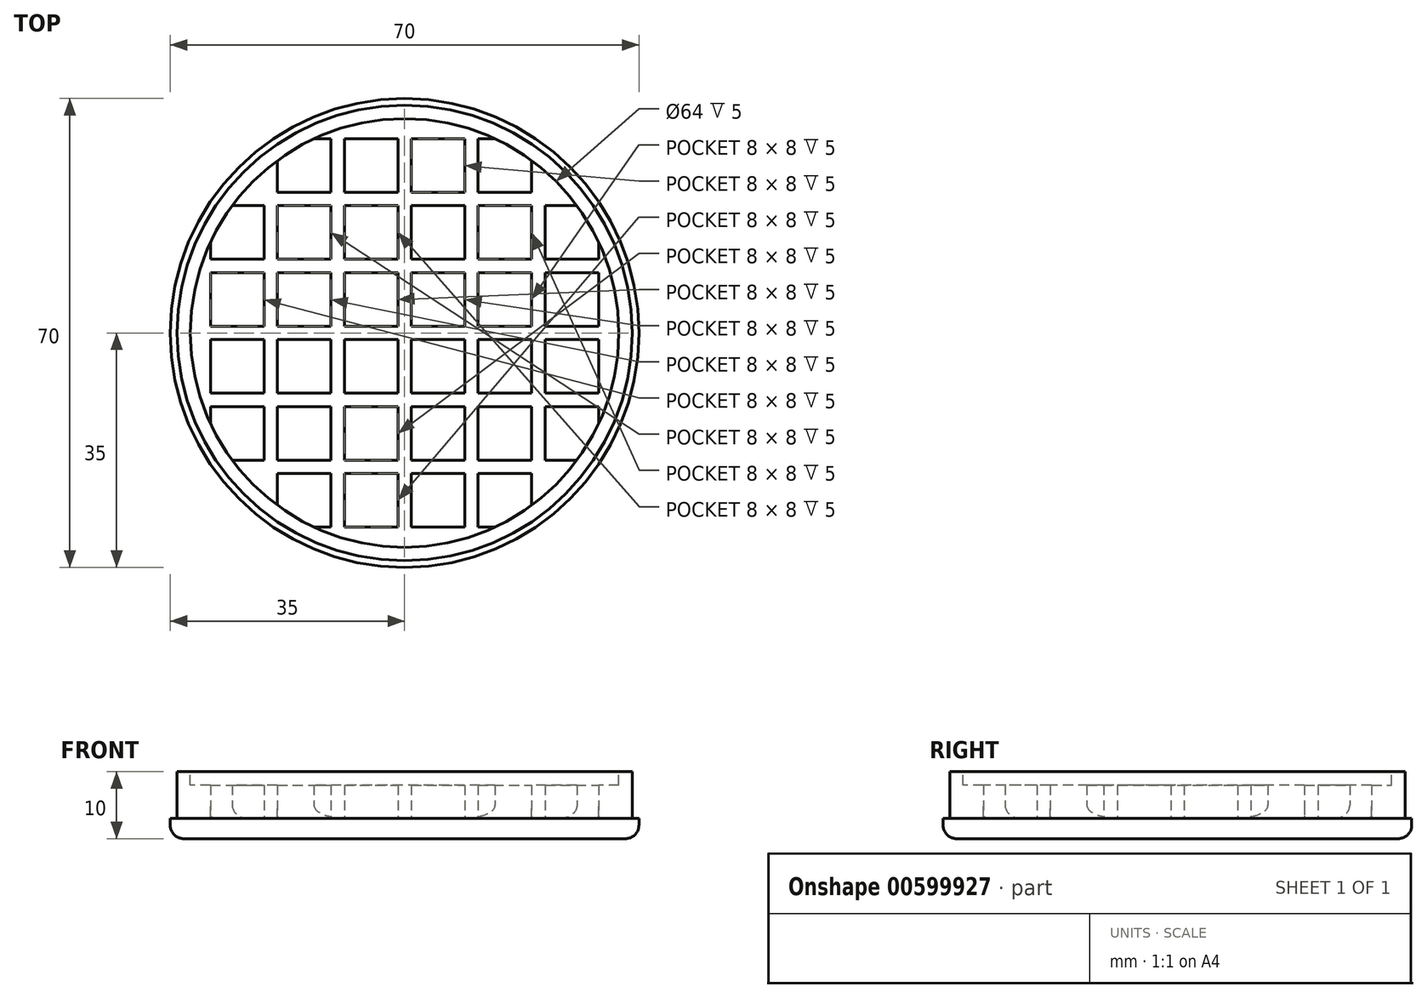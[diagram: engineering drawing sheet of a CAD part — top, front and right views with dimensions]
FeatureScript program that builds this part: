
annotation { "Feature Type Name" : "Feature", "Feature Type Description" : "" }
export const myFeature = defineFeature(function(context is Context, id is Id, definition is map)
    precondition{}
    {
        {
            var Q0;
            Q0=qCreatedBy(makeId("Front.planeOp"),FACE);
            var sketch = newSketch(context, id + "F0", { "sketchPlane" : qUnion([Q0])});
            skLineSegment(sketch, "E0", {"start": v(0, 0) * mm, "end": v(-33, 0) * mm});
            skLineSegment(sketch, "E1", {"start": v(-35, 2) * mm, "end": v(-35, 3) * mm});
            skLineSegment(sketch, "E2", {"start": v(-35, 3) * mm, "end": v(-34, 3) * mm});
            skLineSegment(sketch, "E3", {"start": v(-34, 3) * mm, "end": v(-34, 10) * mm});
            skLineSegment(sketch, "E4", {"start": v(-34, 10) * mm, "end": v(-32, 10) * mm});
            skLineSegment(sketch, "E5", {"start": v(0, 3) * mm, "end": v(0, 0) * mm});
            skPoint(sketch, "E6.visualSharp", {"position": v(-32, 3) * mm});
            skPoint(sketch, "E7.visualSharp", {"position": v(-35, 0) * mm});
            skArc(sketch, "E7.filletArc", {"start": v(-35, 2) * mm, "mid": v(-34.41, 0.59) * mm, "end": v(-33, 0) * mm});
            skLineSegment(sketch, "E8", {"start": v(-32, 10) * mm, "end": v(-32, 3) * mm});
            skLineSegment(sketch, "E9", {"start": v(-32, 3) * mm, "end": v(0, 3) * mm});
            skSolve(sketch);
        }
        {
            var Q0;
            Q0=makeQuery(id+"F0.imprint","IMPRINT",FACE,{"disambiguationData":[TD([[makeQuery(id+"F0.imprint","IMPRINT",EDGE,{"derivedFrom":sQuery(id+"F0.wireOp",EDGE,"E0")}),-1.0]])]});
            var Q1;
            Q1=sQuery(id+"F0.wireOp",EDGE,"E5");
            revolve(context, id + "F1", {"entities" : qUnion([Q0]), "axis" : qUnion([Q1]), "revolveType" : RevolveType.FULL});
        }
        {
            var Q0;
            Q0=makeQuery(id+"F1.opRevolve","SWEPT_FACE",FACE,{"disambiguationData":[OSD([sQuery(id+"F0.wireOp",EDGE,"E9")])]});
            var sketch = newSketch(context, id + "F2", { "sketchPlane" : qUnion([Q0])});
            skLineSegment(sketch, "E10", {"start": v(0, 32) * mm, "end": v(0, 19) * mm, "construction": true});
            skLineSegment(sketch, "E11", {"start": v(-46.87, 0) * mm, "end": v(0, 0) * mm, "construction": true});
            skLineSegment(sketch, "E12.trimOffspring", {"start": v(9, 29) * mm, "end": v(9, 21) * mm});
            skLineSegment(sketch, "E13.trimOffspring", {"start": v(11, 29) * mm, "end": v(13.53, 29) * mm});
            skLineSegment(sketch, "E14.trimOffspring", {"start": v(19, 25.75) * mm, "end": v(19, 21) * mm});
            skLineSegment(sketch, "E15.trimOffspring", {"start": v(29, 13.53) * mm, "end": v(29, 11) * mm});
            skLineSegment(sketch, "E16.trimOffspring", {"start": v(19, 19) * mm, "end": v(19, 11) * mm});
            skLineSegment(sketch, "E17.trimOffspring", {"start": v(21, 19) * mm, "end": v(21, 11) * mm});
            skLineSegment(sketch, "E18.trimOffspring", {"start": v(0, 11) * mm, "end": v(0, -20.11) * mm, "construction": true});
            skLineSegment(sketch, "E19.trimOffspring", {"start": v(11, 19) * mm, "end": v(11, 11) * mm});
            skLineSegment(sketch, "E20.trimOffspring", {"start": v(21, 19) * mm, "end": v(25.75, 19) * mm});
            skLineSegment(sketch, "E21.trimOffspring", {"start": v(9, 9) * mm, "end": v(9, 1) * mm});
            skLineSegment(sketch, "E22.trimOffspring", {"start": v(11, 19) * mm, "end": v(19, 19) * mm});
            skLineSegment(sketch, "E23", {"start": v(11, 29) * mm, "end": v(11, 21) * mm});
            skLineSegment(sketch, "E24.trimOffspring", {"start": v(11, 21) * mm, "end": v(19, 21) * mm});
            skLineSegment(sketch, "E25.trimOffspring", {"start": v(1, 21) * mm, "end": v(9, 21) * mm});
            skLineSegment(sketch, "E26.trimOffspring", {"start": v(1, 19) * mm, "end": v(1, 11) * mm});
            skLineSegment(sketch, "E27.trimOffspring", {"start": v(-1, 19) * mm, "end": v(-1, 11) * mm});
            skLineSegment(sketch, "E28.trimOffspring", {"start": v(1, 19) * mm, "end": v(9, 19) * mm});
            skLineSegment(sketch, "E29.trimOffspring", {"start": v(-9, 21) * mm, "end": v(-1, 21) * mm});
            skLineSegment(sketch, "E30.trimOffspring", {"start": v(-11, 19) * mm, "end": v(-11, 11) * mm});
            skLineSegment(sketch, "E31.trimOffspring", {"start": v(-9, 19) * mm, "end": v(-1, 19) * mm});
            skLineSegment(sketch, "E32.trimOffspring", {"start": v(-9, 19) * mm, "end": v(-9, 11) * mm});
            skLineSegment(sketch, "E33.trimOffspring", {"start": v(-9, 29) * mm, "end": v(-9, 21) * mm});
            skLineSegment(sketch, "E34.trimOffspring", {"start": v(-9, 29) * mm, "end": v(-1, 29) * mm});
            skLineSegment(sketch, "E35.trimOffspring", {"start": v(-11, 29) * mm, "end": v(-11, 21) * mm});
            skLineSegment(sketch, "E36.trimOffspring", {"start": v(-9, 11) * mm, "end": v(-1, 11) * mm});
            skLineSegment(sketch, "E37.trimOffspring", {"start": v(-11, 9) * mm, "end": v(-11, 1) * mm});
            skLineSegment(sketch, "E38.trimOffspring", {"start": v(-9, 9) * mm, "end": v(-9, 1) * mm});
            skLineSegment(sketch, "E39", {"start": v(-19, 9) * mm, "end": v(-11, 9) * mm});
            skLineSegment(sketch, "E40.trimOffspring", {"start": v(-19, 11) * mm, "end": v(-11, 11) * mm});
            skLineSegment(sketch, "E41.trimOffspring", {"start": v(-21, 9) * mm, "end": v(-21, 1) * mm});
            skLineSegment(sketch, "E42.trimOffspring", {"start": v(-19, 9) * mm, "end": v(-19, 1) * mm});
            skLineSegment(sketch, "E43.trimOffspring", {"start": v(-29, 11) * mm, "end": v(-21, 11) * mm});
            skLineSegment(sketch, "E44.trimOffspring", {"start": v(-29, 9) * mm, "end": v(-29, 1) * mm});
            skLineSegment(sketch, "E45.trimOffspring", {"start": v(-29, 9) * mm, "end": v(-21, 9) * mm});
            skLineSegment(sketch, "E46.trimOffspring", {"start": v(-25.75, 19) * mm, "end": v(-21, 19) * mm});
            skLineSegment(sketch, "E47.trimOffspring", {"start": v(-29, 13.53) * mm, "end": v(-29, 11) * mm});
            skPoint(sketch, "E48.MirrorCS.start.orphan", {"position": v(-27.7, 31) * mm});
            skLineSegment(sketch, "E49.trimOffspring", {"start": v(-13.53, 29) * mm, "end": v(-11, 29) * mm});
            skLineSegment(sketch, "E50.trimOffspring", {"start": v(-19, 25.75) * mm, "end": v(-19, 21) * mm});
            skLineSegment(sketch, "E51.trimOffspring", {"start": v(29, -1) * mm, "end": v(29, -9) * mm});
            skLineSegment(sketch, "E52.trimOffspring", {"start": v(29, 9) * mm, "end": v(29, 1) * mm});
            skLineSegment(sketch, "E53.trimOffspring", {"start": v(21, 9) * mm, "end": v(21, 1) * mm});
            skLineSegment(sketch, "E54.trimOffspring", {"start": v(21, 11) * mm, "end": v(29, 11) * mm});
            skLineSegment(sketch, "E55.trimOffspring", {"start": v(19, 9) * mm, "end": v(19, 1) * mm});
            skLineSegment(sketch, "E56.trimOffspring", {"start": v(21, 9) * mm, "end": v(29, 9) * mm});
            skLineSegment(sketch, "E57", {"start": v(9, 11) * mm, "end": v(9, 19) * mm});
            skLineSegment(sketch, "E58.trimOffspring", {"start": v(11, 9) * mm, "end": v(11, 1) * mm});
            skLineSegment(sketch, "E59.trimOffspring", {"start": v(11, 11) * mm, "end": v(19, 11) * mm});
            skLineSegment(sketch, "E60.trimOffspring", {"start": v(11, 9) * mm, "end": v(19, 9) * mm});
            skLineSegment(sketch, "E61.trimOffspring", {"start": v(1, 11) * mm, "end": v(9, 11) * mm});
            skLineSegment(sketch, "E62.trimOffspring", {"start": v(1, 9) * mm, "end": v(9, 9) * mm});
            skLineSegment(sketch, "E63.trimOffspring", {"start": v(1, 9) * mm, "end": v(1, 1) * mm});
            skLineSegment(sketch, "E64.trimOffspring", {"start": v(-1, 9) * mm, "end": v(-1, 1) * mm});
            skLineSegment(sketch, "E65", {"start": v(-19, 21) * mm, "end": v(-11, 21) * mm});
            skLineSegment(sketch, "E66.trimOffspring", {"start": v(-21, 19) * mm, "end": v(-21, 11) * mm});
            skLineSegment(sketch, "E67.trimOffspring", {"start": v(-19, 19) * mm, "end": v(-11, 19) * mm});
            skLineSegment(sketch, "E68.trimOffspring", {"start": v(-19, 19) * mm, "end": v(-19, 11) * mm});
            skLineSegment(sketch, "E69.trimOffspring", {"start": v(-29, 1) * mm, "end": v(-21, 1) * mm});
            skLineSegment(sketch, "E70.trimOffspring", {"start": v(-29, -1) * mm, "end": v(-29, -9) * mm});
            skPoint(sketch, "E71.MirrorCS.start.orphan", {"position": v(-33.6, 29) * mm});
            skLineSegment(sketch, "E72.trimOffspring", {"start": v(-29, -9) * mm, "end": v(-21, -9) * mm});
            skLineSegment(sketch, "E73.trimOffspring", {"start": v(-29, -11) * mm, "end": v(-29, -13.53) * mm});
            skLineSegment(sketch, "E74.trimOffspring", {"start": v(-29, -11) * mm, "end": v(-21, -11) * mm});
            skLineSegment(sketch, "E75.trimOffspring", {"start": v(-25.75, -19) * mm, "end": v(-21, -19) * mm});
            skLineSegment(sketch, "E76.trimOffspring", {"start": v(-13.53, -29) * mm, "end": v(-11, -29) * mm});
            skLineSegment(sketch, "E77.trimOffspring", {"start": v(-19, -21) * mm, "end": v(-11, -21) * mm});
            skLineSegment(sketch, "E78.trimOffspring", {"start": v(-19, -21) * mm, "end": v(-19, -25.75) * mm});
            skLineSegment(sketch, "E79.trimOffspring", {"start": v(-19, -19) * mm, "end": v(-11, -19) * mm});
            skLineSegment(sketch, "E80.trimOffspring", {"start": v(-21, -1) * mm, "end": v(-21, -9) * mm});
            skLineSegment(sketch, "E81.trimOffspring", {"start": v(-19, 1) * mm, "end": v(-11, 1) * mm});
            skLineSegment(sketch, "E82.trimOffspring", {"start": v(-19, -1) * mm, "end": v(-19, -9) * mm});
            skLineSegment(sketch, "E83.trimOffspring", {"start": v(-19, -1) * mm, "end": v(-11, -1) * mm});
            skLineSegment(sketch, "E84.trimOffspring", {"start": v(-11, -1) * mm, "end": v(-11, -9) * mm});
            skLineSegment(sketch, "E85.trimOffspring", {"start": v(-9, -1) * mm, "end": v(-9, -9) * mm});
            skLineSegment(sketch, "E86.trimOffspring", {"start": v(-9, -1) * mm, "end": v(-1, -1) * mm});
            skLineSegment(sketch, "E87.trimOffspring", {"start": v(-1, -11) * mm, "end": v(-1, -19) * mm});
            skLineSegment(sketch, "E88.trimOffspring", {"start": v(1, 1) * mm, "end": v(9, 1) * mm});
            skLineSegment(sketch, "E89.trimOffspring", {"start": v(1, -1) * mm, "end": v(1, -9) * mm});
            skLineSegment(sketch, "E90.trimOffspring", {"start": v(1, -1) * mm, "end": v(9, -1) * mm});
            skLineSegment(sketch, "E91", {"start": v(-9, 9) * mm, "end": v(-1, 9) * mm});
            skLineSegment(sketch, "E92", {"start": v(-9, 1) * mm, "end": v(-1, 1) * mm});
            skLineSegment(sketch, "E93", {"start": v(-1, -1) * mm, "end": v(-1, -9) * mm});
            skLineSegment(sketch, "E94.trimOffspring", {"start": v(1, -9) * mm, "end": v(9, -9) * mm});
            skLineSegment(sketch, "E95.trimOffspring", {"start": v(1, -11) * mm, "end": v(1, -19) * mm});
            skLineSegment(sketch, "E96.trimOffspring", {"start": v(1, -11) * mm, "end": v(9, -11) * mm});
            skLineSegment(sketch, "E97.trimOffspring", {"start": v(-11, -11) * mm, "end": v(-11, -19) * mm});
            skLineSegment(sketch, "E98.trimOffspring", {"start": v(-9, -9) * mm, "end": v(-1, -9) * mm});
            skLineSegment(sketch, "E99.trimOffspring", {"start": v(-9, -11) * mm, "end": v(-9, -19) * mm});
            skLineSegment(sketch, "E100.trimOffspring", {"start": v(-9, -11) * mm, "end": v(-1, -11) * mm});
            skLineSegment(sketch, "E101.trimOffspring", {"start": v(-1, -21) * mm, "end": v(-1, -29) * mm});
            skLineSegment(sketch, "E102.trimOffspring", {"start": v(1, -19) * mm, "end": v(9, -19) * mm});
            skLineSegment(sketch, "E103.trimOffspring", {"start": v(1, -21) * mm, "end": v(1, -29) * mm});
            skLineSegment(sketch, "E104.trimOffspring", {"start": v(1, -21) * mm, "end": v(9, -21) * mm});
            skLineSegment(sketch, "E105.trimOffspring", {"start": v(-9, -19) * mm, "end": v(-1, -19) * mm});
            skLineSegment(sketch, "E106.trimOffspring", {"start": v(-9, -21) * mm, "end": v(-9, -29) * mm});
            skLineSegment(sketch, "E107.trimOffspring", {"start": v(-9, -21) * mm, "end": v(-1, -21) * mm});
            skLineSegment(sketch, "E108.trimOffspring", {"start": v(-11, -21) * mm, "end": v(-11, -29) * mm});
            skLineSegment(sketch, "E109.trimOffspring", {"start": v(-9, -29) * mm, "end": v(-1, -29) * mm});
            skLineSegment(sketch, "E110.trimOffspring", {"start": v(1, -29) * mm, "end": v(9, -29) * mm});
            skLineSegment(sketch, "E111.trimOffspring", {"start": v(-21, -11) * mm, "end": v(-21, -19) * mm});
            skLineSegment(sketch, "E112.trimOffspring", {"start": v(-19, -9) * mm, "end": v(-11, -9) * mm});
            skLineSegment(sketch, "E113.trimOffspring", {"start": v(-19, -11) * mm, "end": v(-19, -19) * mm});
            skLineSegment(sketch, "E114.trimOffspring", {"start": v(-19, -11) * mm, "end": v(-11, -11) * mm});
            skLineSegment(sketch, "E115.trimOffspring", {"start": v(1, 29) * mm, "end": v(1, 21) * mm});
            skLineSegment(sketch, "E116.trimOffspring", {"start": v(1, 29) * mm, "end": v(9, 29) * mm});
            skLineSegment(sketch, "E117.trimOffspring", {"start": v(11, 1) * mm, "end": v(19, 1) * mm});
            skLineSegment(sketch, "E118.trimOffspring", {"start": v(9, -1) * mm, "end": v(9, -9) * mm});
            skLineSegment(sketch, "E119.trimOffspring", {"start": v(11, -1) * mm, "end": v(11, -9) * mm});
            skLineSegment(sketch, "E120.trimOffspring", {"start": v(11, -1) * mm, "end": v(19, -1) * mm});
            skLineSegment(sketch, "E121.trimOffspring", {"start": v(19, -1) * mm, "end": v(19, -9) * mm});
            skLineSegment(sketch, "E122.trimOffspring", {"start": v(21, -1) * mm, "end": v(29, -1) * mm});
            skLineSegment(sketch, "E123.trimOffspring", {"start": v(21, -1) * mm, "end": v(21, -9) * mm});
            skLineSegment(sketch, "E124.trimOffspring", {"start": v(21, 1) * mm, "end": v(29, 1) * mm});
            skLineSegment(sketch, "E125.trimOffspring", {"start": v(29, -11) * mm, "end": v(29, -13.53) * mm});
            skLineSegment(sketch, "E126.trimOffspring", {"start": v(21, -9) * mm, "end": v(29, -9) * mm});
            skLineSegment(sketch, "E127.trimOffspring", {"start": v(19, -11) * mm, "end": v(19, -19) * mm});
            skLineSegment(sketch, "E128.trimOffspring", {"start": v(21, -11) * mm, "end": v(29, -11) * mm});
            skLineSegment(sketch, "E129.trimOffspring", {"start": v(21, -11) * mm, "end": v(21, -19) * mm});
            skLineSegment(sketch, "E130.trimOffspring", {"start": v(21, -19) * mm, "end": v(25.75, -19) * mm});
            skLineSegment(sketch, "E131.trimOffspring", {"start": v(19, -21) * mm, "end": v(19, -25.75) * mm});
            skPoint(sketch, "E132.orphan", {"position": v(21, -41.31) * mm});
            skLineSegment(sketch, "E133.trimOffspring", {"start": v(11, -29) * mm, "end": v(13.53, -29) * mm});
            skLineSegment(sketch, "E134.trimOffspring", {"start": v(11, -19) * mm, "end": v(19, -19) * mm});
            skLineSegment(sketch, "E135.trimOffspring", {"start": v(11, -21) * mm, "end": v(11, -29) * mm});
            skLineSegment(sketch, "E136.trimOffspring", {"start": v(11, -21) * mm, "end": v(19, -21) * mm});
            skLineSegment(sketch, "E137.trimOffspring", {"start": v(9, -21) * mm, "end": v(9, -29) * mm});
            skLineSegment(sketch, "E138.trimOffspring", {"start": v(11, -9) * mm, "end": v(19, -9) * mm});
            skLineSegment(sketch, "E139.trimOffspring", {"start": v(9, -11) * mm, "end": v(9, -19) * mm});
            skLineSegment(sketch, "E140.trimOffspring", {"start": v(11, -11) * mm, "end": v(19, -11) * mm});
            skLineSegment(sketch, "E141.trimOffspring", {"start": v(11, -11) * mm, "end": v(11, -19) * mm});
            skLineSegment(sketch, "E142", {"start": v(-29, -1) * mm, "end": v(-21, -1) * mm});
            skArc(sketch, "E143", {"start": v(25.75, 19) * mm, "mid": v(22.63, 22.63) * mm, "end": v(19, 25.75) * mm});
            skLineSegment(sketch, "E144.trimOffspring", {"start": v(-1, 29) * mm, "end": v(-1, 21) * mm});
            skArc(sketch, "E145.trimOffspring", {"start": v(-29, 13.53) * mm, "mid": v(-32, 0) * mm, "end": v(-29, -13.53) * mm});
            skArc(sketch, "E146.trimOffspring", {"start": v(-19, 25.75) * mm, "mid": v(-22.63, 22.63) * mm, "end": v(-25.75, 19) * mm});
            skArc(sketch, "E147.trimOffspring", {"start": v(13.53, 29) * mm, "mid": v(0, 32) * mm, "end": v(-13.53, 29) * mm});
            skArc(sketch, "E148.1.0", {"start": v(19, -25.75) * mm, "mid": v(22.63, -22.63) * mm, "end": v(25.75, -19) * mm});
            skArc(sketch, "E148.1.1", {"start": v(-25.75, -19) * mm, "mid": v(-22.63, -22.63) * mm, "end": v(-19, -25.75) * mm});
            skArc(sketch, "E148.1.2", {"start": v(29, -13.53) * mm, "mid": v(32, 0) * mm, "end": v(29, 13.53) * mm});
            skArc(sketch, "E149.MirrorCS", {"start": v(13.53, -29) * mm, "mid": v(0, -32) * mm, "end": v(-13.53, -29) * mm});
            skPoint(sketch, "E150.MirrorCS.end.orphan", {"position": v(-13.53, -29) * mm});
            skPoint(sketch, "E150.MirrorCS.start.orphan", {"position": v(13.53, -29) * mm});
            skSolve(sketch);
        }
        {
            var Q0;
            Q0 = qSketchRegion(id + "F2", true);
            extrude(context, id + "F3", {"entities" : qUnion([Q0]), "operationType" : NewBodyOperationType.ADD, "depth" : 5 * mm, "offsetDistance" : 25 * mm});
        }
        {
            var Q0;
            Q0=makeQuery(id+"F3.opExtrude","CAP_EDGE",EDGE,{"disambiguationData":[OSD([sQuery(id+"F2.wireOp",EDGE,"E149.MirrorCS")])],"isStart":false});
            var Q1;
            Q1=makeQuery(id+"F3.opExtrude","CAP_EDGE",EDGE,{"disambiguationData":[OSD([sQuery(id+"F2.wireOp",EDGE,"E148.1.1")])],"isStart":false});
            var Q2;
            Q2=makeQuery(id+"F3.opExtrude","CAP_EDGE",EDGE,{"disambiguationData":[OSD([sQuery(id+"F2.wireOp",EDGE,"E145.trimOffspring")])],"isStart":false});
            var Q3;
            Q3=makeQuery(id+"F3.opExtrude","CAP_EDGE",EDGE,{"disambiguationData":[OSD([sQuery(id+"F2.wireOp",EDGE,"E148.1.0")])],"isStart":false});
            var Q4;
            Q4=makeQuery(id+"F3.opExtrude","CAP_EDGE",EDGE,{"disambiguationData":[OSD([sQuery(id+"F2.wireOp",EDGE,"E148.1.2")])],"isStart":false});
            var Q5;
            Q5=makeQuery(id+"F3.opExtrude","CAP_EDGE",EDGE,{"disambiguationData":[OSD([sQuery(id+"F2.wireOp",EDGE,"E143")])],"isStart":false});
            var Q6;
            Q6=makeQuery(id+"F3.opExtrude","CAP_EDGE",EDGE,{"disambiguationData":[OSD([sQuery(id+"F2.wireOp",EDGE,"E147.trimOffspring")])],"isStart":false});
            var Q7;
            Q7=makeQuery(id+"F3.opExtrude","CAP_EDGE",EDGE,{"disambiguationData":[OSD([sQuery(id+"F2.wireOp",EDGE,"E146.trimOffspring")])],"isStart":false});
            var Q8;
            {var subQ0=sQuery(id+"F0.wireOp",EDGE,"E8");var subQ1=sQuery(id+"F0.wireOp",EDGE,"E9");Q8=makeQuery(id+"F3.boolean.opBoolean","SPLIT",EDGE,{"disambiguationData":[TD([makeQuery(id+"F3.opExtrude","SWEPT_FACE",FACE,{"disambiguationData":[OSD([sQuery(id+"F2.wireOp",EDGE,"E49.trimOffspring")])]})])],"derivedFrom":makeQuery(id+"F1.opRevolve","SWEPT_EDGE",EDGE,{"disambiguationData":[OSD([subQ0,subQ1])]})});}
            var Q9;
            {var subQ0=sQuery(id+"F0.wireOp",EDGE,"E8");var subQ1=sQuery(id+"F0.wireOp",EDGE,"E9");Q9=makeQuery(id+"F3.boolean.opBoolean","SPLIT",EDGE,{"disambiguationData":[TD([makeQuery(id+"F3.opExtrude","SWEPT_FACE",FACE,{"disambiguationData":[OSD([sQuery(id+"F2.wireOp",EDGE,"E46.trimOffspring")])]})])],"derivedFrom":makeQuery(id+"F1.opRevolve","SWEPT_EDGE",EDGE,{"disambiguationData":[OSD([subQ0,subQ1])]})});}
            var Q10;
            {var subQ0=sQuery(id+"F0.wireOp",EDGE,"E8");var subQ1=sQuery(id+"F0.wireOp",EDGE,"E9");Q10=makeQuery(id+"F3.boolean.opBoolean","SPLIT",EDGE,{"disambiguationData":[TD([makeQuery(id+"F3.opExtrude","SWEPT_FACE",FACE,{"disambiguationData":[OSD([sQuery(id+"F2.wireOp",EDGE,"E13.trimOffspring")])]})])],"derivedFrom":makeQuery(id+"F1.opRevolve","SWEPT_EDGE",EDGE,{"disambiguationData":[OSD([subQ0,subQ1])]})});}
            var Q11;
            {var subQ0=sQuery(id+"F0.wireOp",EDGE,"E8");var subQ1=sQuery(id+"F0.wireOp",EDGE,"E9");Q11=makeQuery(id+"F3.boolean.opBoolean","SPLIT",EDGE,{"disambiguationData":[TD([makeQuery(id+"F3.opExtrude","SWEPT_FACE",FACE,{"disambiguationData":[OSD([sQuery(id+"F2.wireOp",EDGE,"E73.trimOffspring")])]})])],"derivedFrom":makeQuery(id+"F1.opRevolve","SWEPT_EDGE",EDGE,{"disambiguationData":[OSD([subQ0,subQ1])]})});}
            var Q12;
            {var subQ0=sQuery(id+"F0.wireOp",EDGE,"E8");var subQ1=sQuery(id+"F0.wireOp",EDGE,"E9");Q12=makeQuery(id+"F3.boolean.opBoolean","SPLIT",EDGE,{"disambiguationData":[TD([makeQuery(id+"F3.opExtrude","SWEPT_FACE",FACE,{"disambiguationData":[OSD([sQuery(id+"F2.wireOp",EDGE,"E76.trimOffspring")])]})])],"derivedFrom":makeQuery(id+"F1.opRevolve","SWEPT_EDGE",EDGE,{"disambiguationData":[OSD([subQ0,subQ1])]})});}
            var Q13;
            {var subQ0=sQuery(id+"F0.wireOp",EDGE,"E8");var subQ1=sQuery(id+"F0.wireOp",EDGE,"E9");Q13=makeQuery(id+"F3.boolean.opBoolean","SPLIT",EDGE,{"disambiguationData":[TD([makeQuery(id+"F3.opExtrude","SWEPT_FACE",FACE,{"disambiguationData":[OSD([sQuery(id+"F2.wireOp",EDGE,"E131.trimOffspring")])]})])],"derivedFrom":makeQuery(id+"F1.opRevolve","SWEPT_EDGE",EDGE,{"disambiguationData":[OSD([subQ0,subQ1])]})});}
            var Q14;
            {var subQ0=sQuery(id+"F0.wireOp",EDGE,"E8");var subQ1=sQuery(id+"F0.wireOp",EDGE,"E9");Q14=makeQuery(id+"F3.boolean.opBoolean","SPLIT",EDGE,{"disambiguationData":[TD([makeQuery(id+"F3.opExtrude","SWEPT_FACE",FACE,{"disambiguationData":[OSD([sQuery(id+"F2.wireOp",EDGE,"E125.trimOffspring")])]})])],"derivedFrom":makeQuery(id+"F1.opRevolve","SWEPT_EDGE",EDGE,{"disambiguationData":[OSD([subQ0,subQ1])]})});}
            var Q15;
            {var subQ0=sQuery(id+"F0.wireOp",EDGE,"E8");var subQ1=sQuery(id+"F0.wireOp",EDGE,"E9");Q15=makeQuery(id+"F3.boolean.opBoolean","SPLIT",EDGE,{"disambiguationData":[TD([makeQuery(id+"F3.opExtrude","SWEPT_FACE",FACE,{"disambiguationData":[OSD([sQuery(id+"F2.wireOp",EDGE,"E15.trimOffspring")])]})])],"derivedFrom":makeQuery(id+"F1.opRevolve","SWEPT_EDGE",EDGE,{"disambiguationData":[OSD([subQ0,subQ1])]})});}
            fillet(context, id + "F4", {"entities" : qUnion([Q0, Q1, Q2, Q3, Q4, Q5, Q6, Q7, Q8, Q9, Q10, Q11, Q12, Q13, Q14, Q15]), "radius" : 2 * mm, "tangentPropagation" : true, "allowEdgeOverflow" : false});
        }
    });
